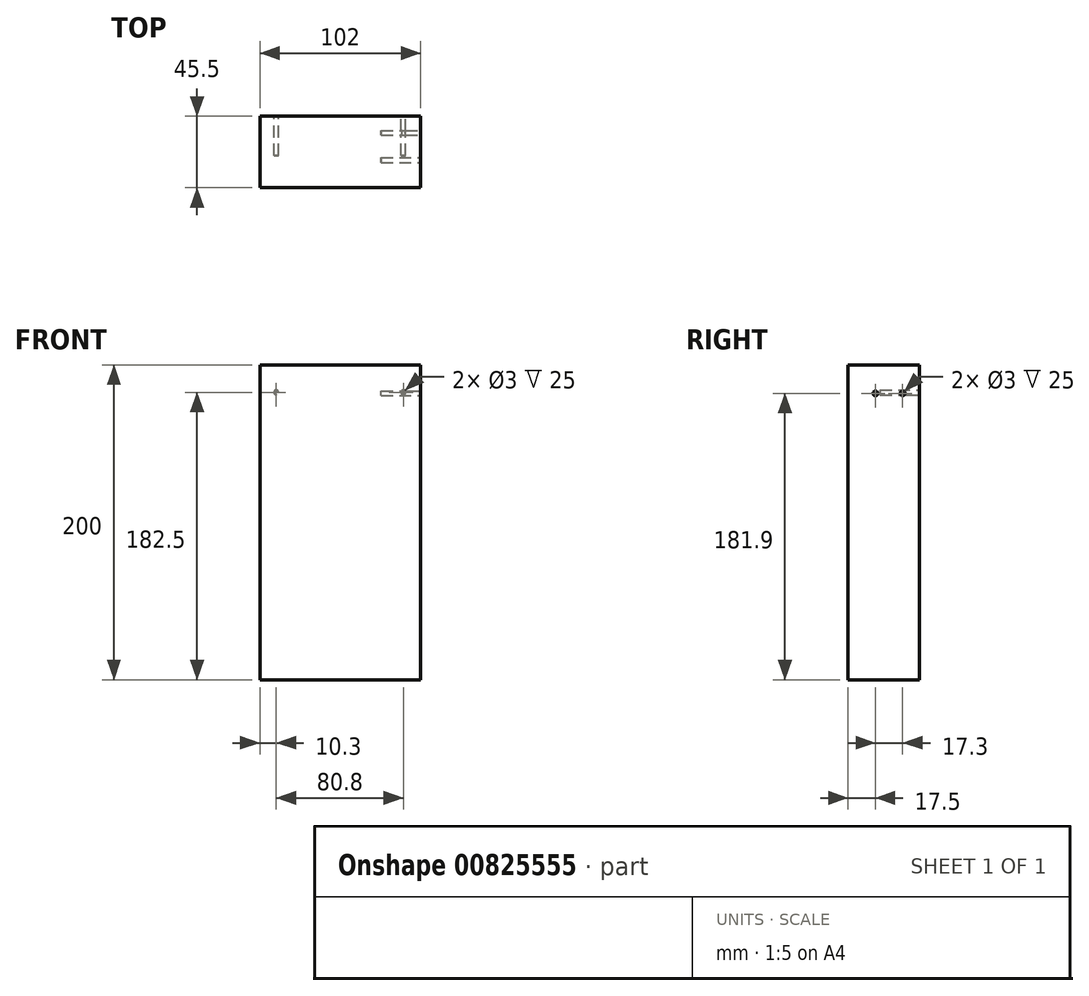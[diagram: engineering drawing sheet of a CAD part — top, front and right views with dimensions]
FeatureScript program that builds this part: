
annotation { "Feature Type Name" : "Feature", "Feature Type Description" : "" }
export const myFeature = defineFeature(function(context is Context, id is Id, definition is map)
    precondition{}
    {
        {
            var Q0;
            Q0=qCreatedBy(makeId("Front.planeOp"),FACE);
            var sketch = newSketch(context, id + "F0", { "sketchPlane" : qUnion([Q0])});
            skLineSegment(sketch, "E0.bottom", {"start": v(51, -100) * mm, "end": v(-51, -100) * mm});
            skLineSegment(sketch, "E0.top", {"start": v(51, 100) * mm, "end": v(-51, 100) * mm});
            skLineSegment(sketch, "E0.left", {"start": v(51, -100) * mm, "end": v(51, 100) * mm});
            skLineSegment(sketch, "E0.right", {"start": v(-51, -100) * mm, "end": v(-51, 100) * mm});
            skPoint(sketch, "E0.middle", {"position": v(0, 0) * mm});
            skSolve(sketch);
        }
        {
            var Q0;
            Q0=makeQuery(id+"F0.imprint","IMPRINT",FACE,{"disambiguationData":[TD([[makeQuery(id+"F0.imprint","IMPRINT",EDGE,{"derivedFrom":sQuery(id+"F0.wireOp",EDGE,"E0.bottom")}),-1.0]])]});
            extrude(context, id + "F1", {"entities" : qUnion([Q0]), "depth" : 45.5 * mm, "offsetDistance" : 25 * mm});
        }
        {
            var Q0;
            Q0=makeQuery(id+"F1.opExtrude","SWEPT_FACE",FACE,{"disambiguationData":[OSD([sQuery(id+"F0.wireOp",EDGE,"E0.left")])]});
            var sketch = newSketch(context, id + "F2", { "sketchPlane" : qUnion([Q0])});
            skCircle(sketch, "E1", {"center": v(-10.7, 81.9) * mm, "radius": 1.5 * mm});
            skCircle(sketch, "E2", {"center": v(-28, 81.9) * mm, "radius": 1.5 * mm});
            skSolve(sketch);
        }
        {
            var Q0;
            Q0=makeQuery(id+"F2.imprint","IMPRINT",FACE,{"disambiguationData":[TD([[makeQuery(id+"F2.imprint","IMPRINT",EDGE,{"derivedFrom":sQuery(id+"F2.wireOp",EDGE,"E2")}),1.0]])]});
            var Q1;
            Q1=makeQuery(id+"F2.imprint","IMPRINT",FACE,{"disambiguationData":[TD([[makeQuery(id+"F2.imprint","IMPRINT",EDGE,{"derivedFrom":sQuery(id+"F2.wireOp",EDGE,"E1")}),1.0]])]});
            extrude(context, id + "F3", {"entities" : qUnion([Q0, Q1]), "operationType" : NewBodyOperationType.REMOVE, "oppositeDirection" : true, "depth" : 25 * mm, "offsetDistance" : 25 * mm});
        }
        {
            var Q0;
            Q0=makeQuery(id+"F1.opExtrude","CAP_FACE",FACE,{"disambiguationData":[OSD([sQuery(id+"F0.wireOp",EDGE,"E0.bottom"),sQuery(id+"F0.wireOp",EDGE,"E0.top"),sQuery(id+"F0.wireOp",EDGE,"E0.left"),sQuery(id+"F0.wireOp",EDGE,"E0.right")])],"isStart":true});
            var sketch = newSketch(context, id + "F4", { "sketchPlane" : qUnion([Q0])});
            skCircle(sketch, "E3", {"center": v(-40.1, 82.5) * mm, "radius": 1.5 * mm});
            skCircle(sketch, "E4", {"center": v(40.7, 82.5) * mm, "radius": 1.5 * mm});
            skSolve(sketch);
        }
        {
            var Q0;
            Q0=makeQuery(id+"F4.imprint","IMPRINT",FACE,{"disambiguationData":[TD([[makeQuery(id+"F4.imprint","IMPRINT",EDGE,{"derivedFrom":sQuery(id+"F4.wireOp",EDGE,"E3")}),1.0]])]});
            var Q1;
            Q1=makeQuery(id+"F4.imprint","IMPRINT",FACE,{"disambiguationData":[TD([[makeQuery(id+"F4.imprint","IMPRINT",EDGE,{"derivedFrom":sQuery(id+"F4.wireOp",EDGE,"E4")}),1.0]])]});
            extrude(context, id + "F5", {"entities" : qUnion([Q0, Q1]), "operationType" : NewBodyOperationType.REMOVE, "oppositeDirection" : true, "depth" : 25 * mm, "offsetDistance" : 25 * mm});
        }
    });
